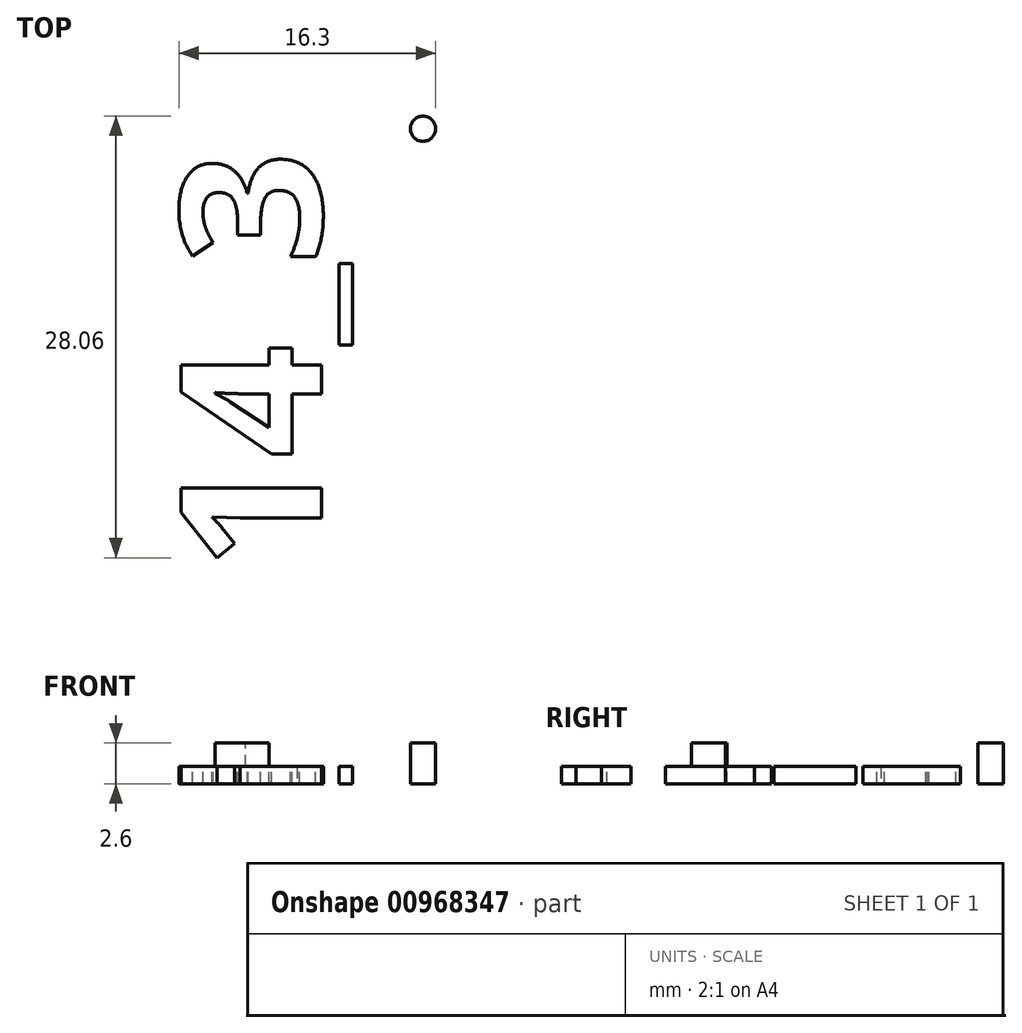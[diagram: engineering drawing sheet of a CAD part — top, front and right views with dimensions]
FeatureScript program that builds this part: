
annotation { "Feature Type Name" : "Feature", "Feature Type Description" : "" }
export const myFeature = defineFeature(function(context is Context, id is Id, definition is map)
    precondition{}
    {
        {
            var Q0;
            Q0=qCreatedBy(makeId("Top.planeOp"),FACE);
            var sketch = newSketch(context, id + "F0", { "sketchPlane" : qUnion([Q0])});
            skLineSegment(sketch, "E0.bottom", {"start": v(-43.16, 48.34) * mm, "end": v(31.84, 48.34) * mm});
            skLineSegment(sketch, "E0.top", {"start": v(-43.16, -21.66) * mm, "end": v(31.84, -21.66) * mm});
            skLineSegment(sketch, "E0.left", {"start": v(-43.16, 48.34) * mm, "end": v(-43.16, -21.66) * mm});
            skLineSegment(sketch, "E0.right", {"start": v(31.84, 48.34) * mm, "end": v(31.84, -21.66) * mm});
            skSolve(sketch);
        }
        {
            var Q0;
            Q0=makeQuery(id+"F0.imprint","IMPRINT",FACE,{"disambiguationData":[TD([[makeQuery(id+"F0.imprint","IMPRINT",EDGE,{"derivedFrom":sQuery(id+"F0.wireOp",EDGE,"E0.bottom")}),-1.0]])]});
            extrude(context, id + "F1", {"entities" : qUnion([Q0]), "depth" : 2.6 * mm, "offsetDistance" : 25 * mm});
        }
        {
            var Q0;
            Q0=makeQuery(id+"F1.opExtrude","CAP_FACE",FACE,{"disambiguationData":[OSD([sQuery(id+"F0.wireOp",EDGE,"E0.bottom"),sQuery(id+"F0.wireOp",EDGE,"E0.top"),sQuery(id+"F0.wireOp",EDGE,"E0.left"),sQuery(id+"F0.wireOp",EDGE,"E0.right")])],"isStart":false});
            var sketch = newSketch(context, id + "F2", { "sketchPlane" : qUnion([Q0])});
            skText(sketch, "E1", { "text": "14_3", "fontName": "OpenSans-Bold.ttf"});
            const initialGuessF2  = {"E1": [-0.02916, -0.00016, 0, 1, 0.009]};
            skSetInitialGuess(sketch, initialGuessF2);
            skSolve(sketch);
        }
        {
            var Q0;
            Q0=qSketchRegion(id+"F2",true);
            extrude(context, id + "F3", {"entities" : qUnion([Q0]), "operationType" : NewBodyOperationType.REMOVE, "oppositeDirection" : true, "depth" : 1.5 * mm, "offsetDistance" : 25 * mm});
        }
        {
            var Q0;
            {var subQ0=sQuery(id+"F0.wireOp",EDGE,"E0.left");var subQ1=sQuery(id+"F0.wireOp",EDGE,"E0.bottom");var subQ2=sQuery(id+"F0.wireOp",EDGE,"E0.right");var subQ3=sQuery(id+"F0.wireOp",EDGE,"E0.top");Q0=makeQuery(id+"F3.boolean.opBoolean","SPLIT",FACE,{"disambiguationData":[TD([makeQuery(id+"F1.opExtrude","SWEPT_FACE",FACE,{"disambiguationData":[OSD([subQ1])]})])],"derivedFrom":makeQuery(id+"F1.opExtrude","CAP_FACE",FACE,{"disambiguationData":[OSD([subQ1,subQ3,subQ0,subQ2])],"isStart":false})});}
            var sketch = newSketch(context, id + "F4", { "sketchPlane" : qUnion([Q0])});
            skLineSegment(sketch, "E2.bottom", {"start": v(-23.16, -19.81) * mm, "end": v(27.84, -19.81) * mm});
            skLineSegment(sketch, "E2.top", {"start": v(-23.16, 46.49) * mm, "end": v(27.84, 46.49) * mm});
            skLineSegment(sketch, "E2.left", {"start": v(-23.16, -19.81) * mm, "end": v(-23.16, 46.49) * mm});
            skLineSegment(sketch, "E2.right", {"start": v(27.84, -19.81) * mm, "end": v(27.84, 46.49) * mm});
            skCircle(sketch, "E3", {"center": v(-22.7, 16.34) * mm, "radius": 0.8 * mm});
            skCircle(sketch, "E4", {"center": v(-22.7, 27.84) * mm, "radius": 0.8 * mm});
            skCircle(sketch, "E5", {"center": v(8.1, 31.39) * mm, "radius": 0.8 * mm});
            skSolve(sketch);
        }
        {
            var Q0;
            {var subQ0=sQuery(id+"F4.wireOp",EDGE,"E3");var subQ1=sQuery(id+"F4.wireOp",EDGE,"E2.left");var subQ2=makeQuery(id+"F4.imprint","INTERSECT",VERTEX,{"disambiguationData":[OD(0.0)],"derivedFrom":[subQ1,subQ0]});Q0=makeQuery(id+"F4.imprint","IMPRINT",FACE,{"disambiguationData":[TD([[makeQuery(id+"F4.imprint","IMPRINT",EDGE,{"disambiguationData":[TD([[subQ2,-1.0]])],"derivedFrom":subQ1}),1.0]])]});}
            var Q1;
            {var subQ0=sQuery(id+"F4.wireOp",EDGE,"E3");var subQ1=sQuery(id+"F4.wireOp",EDGE,"E2.left");var subQ2=makeQuery(id+"F4.imprint","INTERSECT",VERTEX,{"disambiguationData":[OD(0.0)],"derivedFrom":[subQ1,subQ0]});Q1=makeQuery(id+"F4.imprint","IMPRINT",FACE,{"disambiguationData":[TD([[makeQuery(id+"F4.imprint","IMPRINT",EDGE,{"disambiguationData":[TD([[subQ2,-1.0]])],"derivedFrom":subQ1}),-1.0]])]});}
            var Q2;
            {var subQ0=sQuery(id+"F4.wireOp",EDGE,"E4");var subQ1=sQuery(id+"F4.wireOp",EDGE,"E2.left");var subQ2=makeQuery(id+"F4.imprint","INTERSECT",VERTEX,{"disambiguationData":[OD(0.0)],"derivedFrom":[subQ1,subQ0]});Q2=makeQuery(id+"F4.imprint","IMPRINT",FACE,{"disambiguationData":[TD([[makeQuery(id+"F4.imprint","IMPRINT",EDGE,{"disambiguationData":[TD([[subQ2,-1.0]])],"derivedFrom":subQ1}),1.0]])]});}
            var Q3;
            {var subQ0=sQuery(id+"F4.wireOp",EDGE,"E4");var subQ1=sQuery(id+"F4.wireOp",EDGE,"E2.left");var subQ2=makeQuery(id+"F4.imprint","INTERSECT",VERTEX,{"disambiguationData":[OD(0.0)],"derivedFrom":[subQ1,subQ0]});Q3=makeQuery(id+"F4.imprint","IMPRINT",FACE,{"disambiguationData":[TD([[makeQuery(id+"F4.imprint","IMPRINT",EDGE,{"disambiguationData":[TD([[subQ2,-1.0]])],"derivedFrom":subQ1}),-1.0]])]});}
            var Q4;
            Q4=makeQuery(id+"F4.imprint","IMPRINT",FACE,{"disambiguationData":[TD([[makeQuery(id+"F4.imprint","IMPRINT",EDGE,{"derivedFrom":sQuery(id+"F4.wireOp",EDGE,"E5")}),1.0]])]});
            extrude(context, id + "F5", {"entities" : qUnion([Q0, Q1, Q2, Q3, Q4]), "operationType" : NewBodyOperationType.REMOVE, "endBound" : BoundingType.UP_TO_NEXT, "oppositeDirection" : true, "depth" : 25 * mm, "offsetDistance" : 25 * mm});
        }
    });
